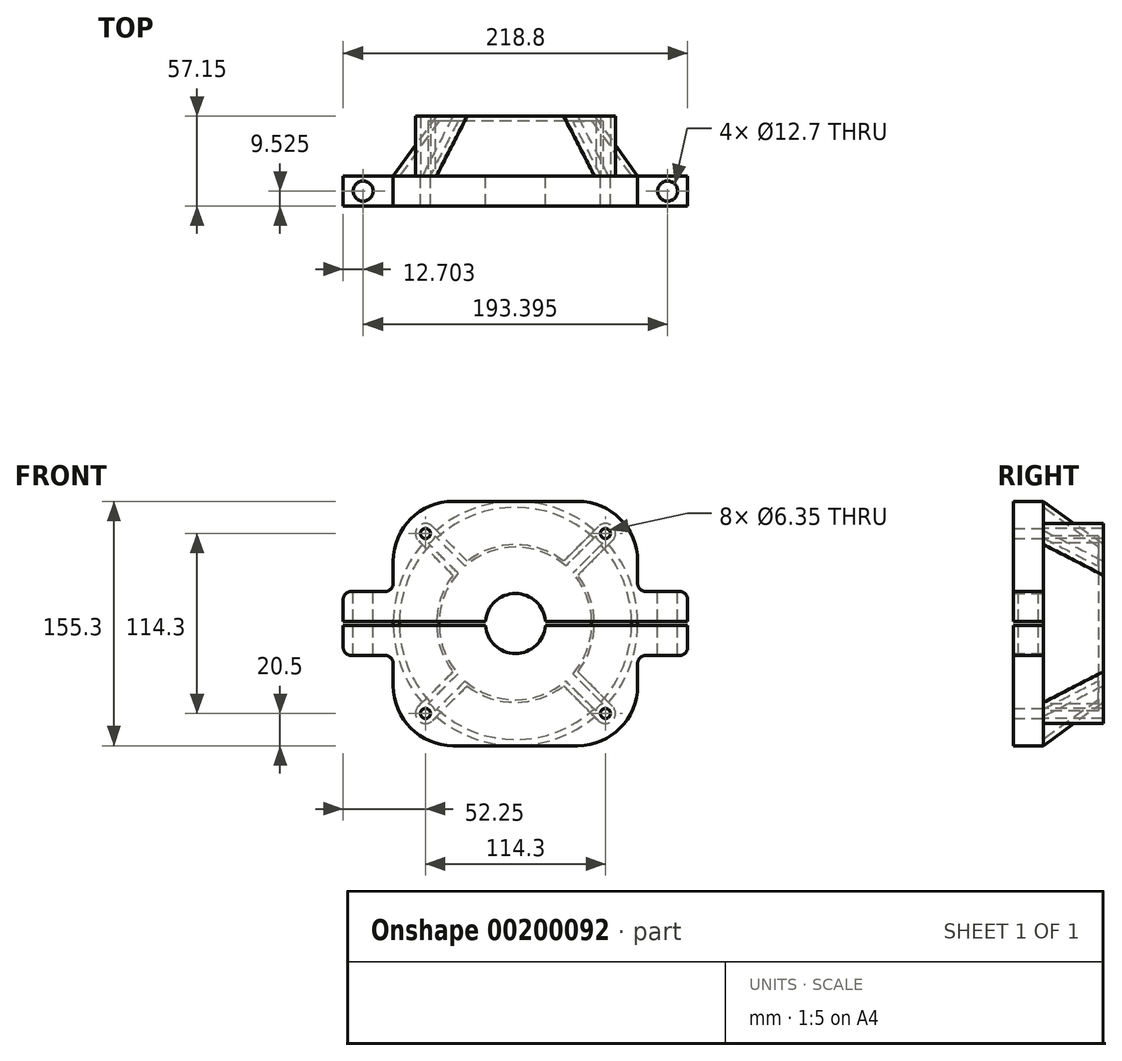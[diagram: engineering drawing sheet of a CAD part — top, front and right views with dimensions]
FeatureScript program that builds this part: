
annotation { "Feature Type Name" : "Feature", "Feature Type Description" : "" }
export const myFeature = defineFeature(function(context is Context, id is Id, definition is map)
    precondition{}
    {
        {
            var Q0;
            Q0=qCreatedBy(makeId("Front.planeOp"),FACE);
            var sketch = newSketch(context, id + "F0", { "sketchPlane" : qUnion([Q0])});
            skLineSegment(sketch, "E0.bottom", {"start": v(57.15, 57.15) * mm, "end": v(-57.15, 57.15) * mm, "construction": true});
            skLineSegment(sketch, "E0.top", {"start": v(57.15, -57.15) * mm, "end": v(-57.15, -57.15) * mm, "construction": true});
            skLineSegment(sketch, "E0.left", {"start": v(57.15, 57.15) * mm, "end": v(57.15, -57.15) * mm, "construction": true});
            skLineSegment(sketch, "E0.right", {"start": v(-57.15, 57.15) * mm, "end": v(-57.15, -57.15) * mm, "construction": true});
            skCircle(sketch, "E1", {"center": v(0, 0) * mm, "radius": 77.65 * mm});
            skCircle(sketch, "E2", {"center": v(-57.15, 57.15) * mm, "radius": 6.35 * mm, "construction": true});
            skCircle(sketch, "E3", {"center": v(57.15, 57.15) * mm, "radius": 6.35 * mm, "construction": true});
            skCircle(sketch, "E4", {"center": v(-57.15, -57.15) * mm, "radius": 6.35 * mm, "construction": true});
            skCircle(sketch, "E5", {"center": v(57.15, -57.15) * mm, "radius": 6.35 * mm, "construction": true});
            skLineSegment(sketch, "E6", {"start": v(-57.15, 57.15) * mm, "end": v(57.15, -57.15) * mm, "construction": true});
            skSolve(sketch);
        }
        {
            var Q0;
            Q0=qCreatedBy(makeId("Front.planeOp"),FACE);
            cPlane(context, id + "F1", {"entities" : qUnion([Q0]), "cplaneType" : CPlaneType.OFFSET, "offset" : 38.1 * mm, "oppositeDirection" : true, "width" : 152.4 * mm, "height" : 152.4 * mm});
        }
        {
            var Q0;
            Q0=qCreatedBy(id+"F1.planeOp",FACE);
            var sketch = newSketch(context, id + "F2", { "sketchPlane" : qUnion([Q0])});
            skCircle(sketch, "E7", {"center": v(0, 0) * mm, "radius": 50.09 * mm});
            skSolve(sketch);
        }
        {
            var Q0;
            Q0 = qSketchRegion(id + "F0", true);
            var Q1;
            Q1 = qSketchRegion(id + "F2", true);
            loft(context, id + "F3", {"sheetProfilesArray" : [{ "sheetProfileEntities" : qUnion([Q0]) }, { "sheetProfileEntities" : qUnion([Q1]) }]});
        }
        {
            var Q0;
            Q0=qCreatedBy(makeId("Front.planeOp"),FACE);
            var sketch = newSketch(context, id + "F4", { "sketchPlane" : qUnion([Q0])});
            skArc(sketch, "E8.0", {"start": v(-52.66, 61.64) * mm, "mid": v(-61.64, 61.64) * mm, "end": v(-61.64, 52.66) * mm});
            skArc(sketch, "E8.1", {"start": v(61.64, 52.66) * mm, "mid": v(61.64, 61.64) * mm, "end": v(52.66, 61.64) * mm});
            skArc(sketch, "E8.2", {"start": v(-61.64, -52.66) * mm, "mid": v(-61.64, -61.64) * mm, "end": v(-52.66, -61.64) * mm});
            skArc(sketch, "E8.3", {"start": v(52.66, -61.64) * mm, "mid": v(61.64, -61.64) * mm, "end": v(61.64, -52.66) * mm});
            skLineSegment(sketch, "E9", {"start": v(-61.64, 52.66) * mm, "end": v(-8.98, 0) * mm});
            skLineSegment(sketch, "E10", {"start": v(-52.66, 61.64) * mm, "end": v(0, 8.98) * mm});
            skLineSegment(sketch, "E11", {"start": v(-61.64, -52.66) * mm, "end": v(-8.98, 0) * mm});
            skLineSegment(sketch, "E12", {"start": v(-52.66, -61.64) * mm, "end": v(0, -8.98) * mm});
            skLineSegment(sketch, "E13.trimOffspring", {"start": v(0, -8.98) * mm, "end": v(52.66, -61.64) * mm});
            skLineSegment(sketch, "E14.trimOffspring", {"start": v(0, 8.98) * mm, "end": v(52.66, 61.64) * mm});
            skLineSegment(sketch, "E15.trimOffspring", {"start": v(8.98, 0) * mm, "end": v(61.64, -52.66) * mm});
            skLineSegment(sketch, "E16.trimOffspring", {"start": v(8.98, 0) * mm, "end": v(61.64, 52.66) * mm});
            skCircle(sketch, "E17", {"center": v(-57.15, 57.15) * mm, "radius": 3.18 * mm});
            skCircle(sketch, "E18", {"center": v(57.15, 57.15) * mm, "radius": 3.18 * mm});
            skCircle(sketch, "E19", {"center": v(-57.15, -57.15) * mm, "radius": 3.18 * mm});
            skCircle(sketch, "E20", {"center": v(57.15, -57.15) * mm, "radius": 3.18 * mm});
            skSolve(sketch);
        }
        {
            var Q0;
            Q0 = qSketchRegion(id + "F4", true);
            var Q1;
            Q1=makeQuery(id+"F3.opLoft","CAP_FACE",FACE,{"disambiguationData":[OSD([makeQuery(id+"F2.imprint","IMPRINT",FACE,{"disambiguationData":[TD([[makeQuery(id+"F2.imprint","IMPRINT",EDGE,{"derivedFrom":sQuery(id+"F2.wireOp",EDGE,"E7")}),1.0]])]})])],"isStart":true});
            extrude(context, id + "F5", {"entities" : qUnion([Q0]), "operationType" : NewBodyOperationType.ADD, "endBound" : BoundingType.UP_TO_SURFACE, "oppositeDirection" : true, "endBoundEntityFace" : qUnion([Q1]), "depth" : 25.4 * mm});
        }
        {
            var Q0;
            Q0=makeQuery(id+"F5.boolean.opBoolean","MERGE",FACE,{"derivedFrom":[makeQuery(id+"F3.opLoft","CAP_FACE",FACE,{"disambiguationData":[OSD([makeQuery(id+"F0.imprint","IMPRINT",FACE,{"disambiguationData":[TD([[makeQuery(id+"F0.imprint","IMPRINT",EDGE,{"derivedFrom":sQuery(id+"F0.wireOp",EDGE,"E1")}),1.0]])]})])],"isStart":true}),makeQuery(id+"F5.opExtrude","CAP_FACE",FACE,{"disambiguationData":[OSD([sQuery(id+"F4.wireOp",EDGE,"E8.0"),sQuery(id+"F4.wireOp",EDGE,"E8.1"),sQuery(id+"F4.wireOp",EDGE,"E8.2"),sQuery(id+"F4.wireOp",EDGE,"E8.3"),sQuery(id+"F4.wireOp",EDGE,"E9"),sQuery(id+"F4.wireOp",EDGE,"E10"),sQuery(id+"F4.wireOp",EDGE,"E11"),sQuery(id+"F4.wireOp",EDGE,"E12"),sQuery(id+"F4.wireOp",EDGE,"E13.trimOffspring"),sQuery(id+"F4.wireOp",EDGE,"E14.trimOffspring"),sQuery(id+"F4.wireOp",EDGE,"E15.trimOffspring"),sQuery(id+"F4.wireOp",EDGE,"E16.trimOffspring"),sQuery(id+"F4.wireOp",EDGE,"E17"),sQuery(id+"F4.wireOp",EDGE,"E18"),sQuery(id+"F4.wireOp",EDGE,"E19"),sQuery(id+"F4.wireOp",EDGE,"E20")])],"isStart":true})]});
            shell(context, id + "F6", {"entities" : qUnion([Q0]), "thickness" : 3.17 * mm});
        }
        {
            var Q0;
            Q0=qCreatedBy(makeId("Front.planeOp"),FACE);
            var sketch = newSketch(context, id + "F7", { "sketchPlane" : qUnion([Q0])});
            skArc(sketch, "E21", {"start": v(19, 1.27) * mm, "mid": v(0, 19.05) * mm, "end": v(-19, 1.27) * mm});
            skLineSegment(sketch, "E22.bottom", {"start": v(77.65, 77.65) * mm, "end": v(-77.65, 77.65) * mm});
            skLineSegment(sketch, "E22.top", {"start": v(77.65, -77.65) * mm, "end": v(-77.65, -77.65) * mm});
            skLineSegment(sketch, "E22.left", {"start": v(77.65, 77.65) * mm, "end": v(77.65, 20.32) * mm});
            skLineSegment(sketch, "E22.right", {"start": v(-77.65, 77.65) * mm, "end": v(-77.65, 20.32) * mm});
            skLineSegment(sketch, "E23.bottom", {"start": v(77.65, 1.27) * mm, "end": v(19, 1.27) * mm});
            skLineSegment(sketch, "E23.top", {"start": v(77.65, -1.27) * mm, "end": v(19, -1.27) * mm});
            skLineSegment(sketch, "E24.trimOffspring", {"start": v(-19, 1.27) * mm, "end": v(-77.65, 1.27) * mm});
            skArc(sketch, "E25.trimOffspring", {"start": v(-19, -1.27) * mm, "mid": v(0, -19.05) * mm, "end": v(19, -1.27) * mm});
            skLineSegment(sketch, "E26.trimOffspring", {"start": v(-19, -1.27) * mm, "end": v(-77.65, -1.27) * mm});
            skLineSegment(sketch, "E27.trimOffspring", {"start": v(-77.65, -20.32) * mm, "end": v(-77.65, -77.65) * mm});
            skLineSegment(sketch, "E28.trimOffspring", {"start": v(77.65, -20.32) * mm, "end": v(77.65, -77.65) * mm});
            skLineSegment(sketch, "E29.bottom", {"start": v(-77.65, 1.27) * mm, "end": v(-109.4, 1.27) * mm});
            skLineSegment(sketch, "E29.top", {"start": v(-77.65, 20.32) * mm, "end": v(-109.4, 20.32) * mm});
            skLineSegment(sketch, "E29.right", {"start": v(-109.4, 1.27) * mm, "end": v(-109.4, 20.32) * mm});
            skLineSegment(sketch, "E30.bottom", {"start": v(-77.65, -1.27) * mm, "end": v(-109.4, -1.27) * mm});
            skLineSegment(sketch, "E30.top", {"start": v(-77.65, -20.32) * mm, "end": v(-109.4, -20.32) * mm});
            skLineSegment(sketch, "E30.right", {"start": v(-109.4, -1.27) * mm, "end": v(-109.4, -20.32) * mm});
            skLineSegment(sketch, "E31.bottom", {"start": v(77.65, 1.27) * mm, "end": v(109.4, 1.27) * mm});
            skLineSegment(sketch, "E31.top", {"start": v(77.65, 20.32) * mm, "end": v(109.4, 20.32) * mm});
            skLineSegment(sketch, "E31.right", {"start": v(109.4, 1.27) * mm, "end": v(109.4, 20.32) * mm});
            skLineSegment(sketch, "E32.bottom", {"start": v(77.65, -1.27) * mm, "end": v(109.4, -1.27) * mm});
            skLineSegment(sketch, "E32.top", {"start": v(77.65, -20.32) * mm, "end": v(109.4, -20.32) * mm});
            skLineSegment(sketch, "E32.right", {"start": v(109.4, -1.27) * mm, "end": v(109.4, -20.32) * mm});
            skCircle(sketch, "E33.0", {"center": v(-57.15, 57.15) * mm, "radius": 3.18 * mm});
            skCircle(sketch, "E34.0", {"center": v(57.15, 57.15) * mm, "radius": 3.18 * mm});
            skCircle(sketch, "E35.0", {"center": v(-57.15, -57.15) * mm, "radius": 3.18 * mm});
            skCircle(sketch, "E36.0", {"center": v(57.15, -57.15) * mm, "radius": 3.18 * mm});
            skSolve(sketch);
        }
        {
            var Q0;
            Q0 = qSketchRegion(id + "F7", true);
            extrude(context, id + "F8", {"entities" : qUnion([Q0]), "depth" : 19.05 * mm});
        }
        {
            var Q0;
            Q0=makeQuery(id+"F8.opExtrude","SWEPT_FACE",FACE,{"disambiguationData":[OSD([sQuery(id+"F7.wireOp",EDGE,"E22.bottom")])]});
            var sketch = newSketch(context, id + "F9", { "sketchPlane" : qUnion([Q0])});
            skCircle(sketch, "E37", {"center": v(-96.7, -9.53) * mm, "radius": 6.35 * mm});
            skCircle(sketch, "E38", {"center": v(96.7, -9.53) * mm, "radius": 6.35 * mm});
            skLineSegment(sketch, "E39", {"start": v(-96.7, -9.53) * mm, "end": v(-109.4, -9.53) * mm, "construction": true});
            skLineSegment(sketch, "E40", {"start": v(96.7, -9.53) * mm, "end": v(109.4, -9.53) * mm, "construction": true});
            skSolve(sketch);
        }
        {
            var Q0;
            Q0 = qSketchRegion(id + "F9", true);
            extrude(context, id + "F10", {"entities" : qUnion([Q0]), "operationType" : NewBodyOperationType.REMOVE, "endBound" : BoundingType.THROUGH_ALL, "oppositeDirection" : true, "depth" : 25.4 * mm});
        }
        {
            var Q0;
            Q0=makeQuery(id+"F8.opExtrude","SWEPT_EDGE",EDGE,{"disambiguationData":[OSD([sQuery(id+"F7.wireOp",EDGE,"E22.bottom"),sQuery(id+"F7.wireOp",EDGE,"E22.right")])]});
            var Q1;
            Q1=makeQuery(id+"F8.opExtrude","SWEPT_EDGE",EDGE,{"disambiguationData":[OSD([sQuery(id+"F7.wireOp",EDGE,"E22.bottom"),sQuery(id+"F7.wireOp",EDGE,"E22.left")])]});
            var Q2;
            Q2=makeQuery(id+"F8.opExtrude","SWEPT_EDGE",EDGE,{"disambiguationData":[OSD([sQuery(id+"F7.wireOp",EDGE,"E22.top"),sQuery(id+"F7.wireOp",EDGE,"E27.trimOffspring")])]});
            var Q3;
            Q3=makeQuery(id+"F8.opExtrude","SWEPT_EDGE",EDGE,{"disambiguationData":[OSD([sQuery(id+"F7.wireOp",EDGE,"E22.top"),sQuery(id+"F7.wireOp",EDGE,"E28.trimOffspring")])]});
            fillet(context, id + "F11", {"entities" : qUnion([Q0, Q1, Q2, Q3]), "radius" : 38.1 * mm, "tangentPropagation" : true, "allowEdgeOverflow" : false});
        }
        {
            var Q0;
            Q0=makeQuery(id+"F8.opExtrude","SWEPT_EDGE",EDGE,{"disambiguationData":[OSD([sQuery(id+"F7.wireOp",EDGE,"E22.right"),sQuery(id+"F7.wireOp",EDGE,"E29.top")])]});
            var Q1;
            Q1=makeQuery(id+"F8.opExtrude","SWEPT_EDGE",EDGE,{"disambiguationData":[OSD([sQuery(id+"F7.wireOp",EDGE,"E29.top"),sQuery(id+"F7.wireOp",EDGE,"E29.right")])]});
            var Q2;
            Q2=makeQuery(id+"F8.opExtrude","SWEPT_EDGE",EDGE,{"disambiguationData":[OSD([sQuery(id+"F7.wireOp",EDGE,"E30.top"),sQuery(id+"F7.wireOp",EDGE,"E30.right")])]});
            var Q3;
            Q3=makeQuery(id+"F8.opExtrude","SWEPT_EDGE",EDGE,{"disambiguationData":[OSD([sQuery(id+"F7.wireOp",EDGE,"E27.trimOffspring"),sQuery(id+"F7.wireOp",EDGE,"E30.top")])]});
            var Q4;
            Q4=makeQuery(id+"F8.opExtrude","SWEPT_EDGE",EDGE,{"disambiguationData":[OSD([sQuery(id+"F7.wireOp",EDGE,"E22.left"),sQuery(id+"F7.wireOp",EDGE,"E31.top")])]});
            var Q5;
            Q5=makeQuery(id+"F8.opExtrude","SWEPT_EDGE",EDGE,{"disambiguationData":[OSD([sQuery(id+"F7.wireOp",EDGE,"E31.top"),sQuery(id+"F7.wireOp",EDGE,"E31.right")])]});
            var Q6;
            Q6=makeQuery(id+"F8.opExtrude","SWEPT_EDGE",EDGE,{"disambiguationData":[OSD([sQuery(id+"F7.wireOp",EDGE,"E28.trimOffspring"),sQuery(id+"F7.wireOp",EDGE,"E32.top")])]});
            var Q7;
            Q7=makeQuery(id+"F8.opExtrude","SWEPT_EDGE",EDGE,{"disambiguationData":[OSD([sQuery(id+"F7.wireOp",EDGE,"E32.top"),sQuery(id+"F7.wireOp",EDGE,"E32.right")])]});
            fillet(context, id + "F12", {"entities" : qUnion([Q0, Q1, Q2, Q3, Q4, Q5, Q6, Q7]), "radius" : 5.08 * mm, "tangentPropagation" : true, "allowEdgeOverflow" : false});
        }
    });
